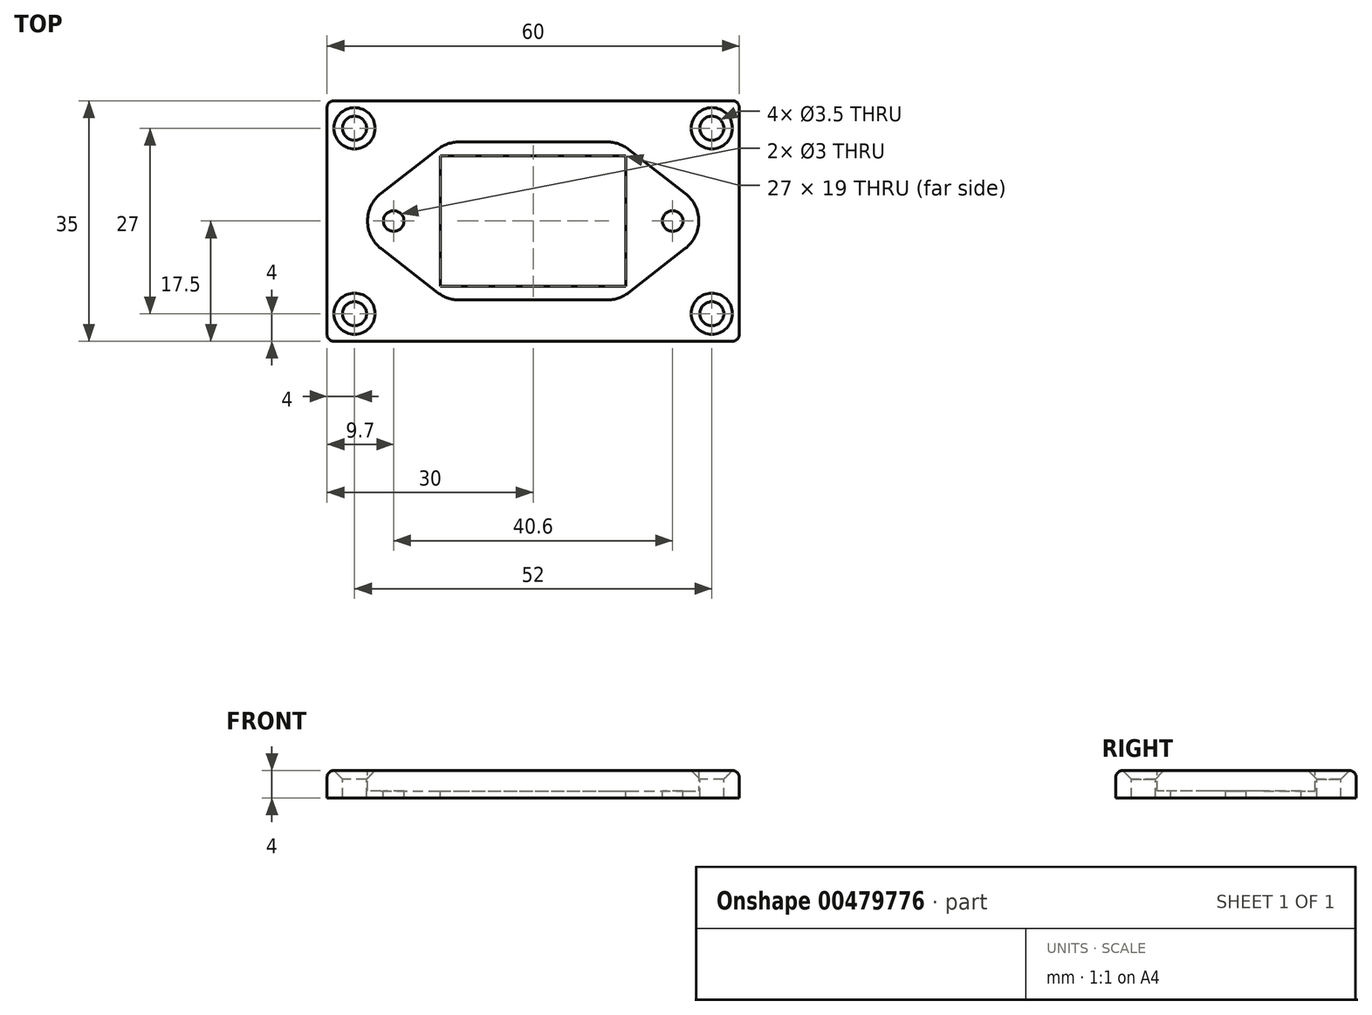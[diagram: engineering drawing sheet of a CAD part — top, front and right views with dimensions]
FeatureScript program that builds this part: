
annotation { "Feature Type Name" : "Feature", "Feature Type Description" : "" }
export const myFeature = defineFeature(function(context is Context, id is Id, definition is map)
    precondition{}
    {
        {
            var Q0;
            Q0=qCreatedBy(makeId("Top.planeOp"),FACE);
            var sketch = newSketch(context, id + "F0", { "sketchPlane" : qUnion([Q0])});
            skLineSegment(sketch, "E0.bottom", {"start": v(-30, 17.5) * mm, "end": v(30, 17.5) * mm});
            skLineSegment(sketch, "E0.top", {"start": v(-30, -17.5) * mm, "end": v(30, -17.5) * mm});
            skLineSegment(sketch, "E0.left", {"start": v(-30, 17.5) * mm, "end": v(-30, -17.5) * mm});
            skLineSegment(sketch, "E0.right", {"start": v(30, 17.5) * mm, "end": v(30, -17.5) * mm});
            skSolve(sketch);
        }
        {
            var Q0;
            Q0 = qSketchRegion(id + "F0", true);
            extrude(context, id + "F1", {"entities" : qUnion([Q0]), "depth" : 4 * mm});
        }
        {
            var Q0;
            Q0=makeQuery(id+"F1.opExtrude","CAP_FACE",FACE,{"disambiguationData":[OSD([sQuery(id+"F0.wireOp",EDGE,"E0.bottom"),sQuery(id+"F0.wireOp",EDGE,"E0.top"),sQuery(id+"F0.wireOp",EDGE,"E0.left"),sQuery(id+"F0.wireOp",EDGE,"E0.right")])],"isStart":false});
            var sketch = newSketch(context, id + "F2", { "sketchPlane" : qUnion([Q0])});
            skLineSegment(sketch, "E1", {"start": v(-12.5, -11.5) * mm, "end": v(12.5, -11.5) * mm});
            skLineSegment(sketch, "E2", {"start": v(-12.5, 11.5) * mm, "end": v(12.5, 11.5) * mm});
            skLineSegment(sketch, "E3", {"start": v(12.5, -11.5) * mm, "end": v(27.3, 0) * mm});
            skLineSegment(sketch, "E4", {"start": v(27.3, 0) * mm, "end": v(12.5, 11.5) * mm});
            skLineSegment(sketch, "E5", {"start": v(-27.3, 0) * mm, "end": v(-12.5, 11.5) * mm});
            skLineSegment(sketch, "E6", {"start": v(-27.3, 0) * mm, "end": v(-12.5, -11.5) * mm});
            skSolve(sketch);
        }
        {
            var Q0;
            Q0 = qSketchRegion(id + "F2", true);
            extrude(context, id + "F3", {"entities" : qUnion([Q0]), "operationType" : NewBodyOperationType.REMOVE, "oppositeDirection" : true, "depth" : 3 * mm});
        }
        {
            var Q0;
            Q0=makeQuery(id+"F3.boolean.opBoolean","COPY",EDGE,{"derivedFrom":makeQuery(id+"F3.opExtrude","SWEPT_EDGE",EDGE,{"disambiguationData":[OSD([sQuery(id+"F2.wireOp",EDGE,"E2"),sQuery(id+"F2.wireOp",EDGE,"E4")])]})});
            var Q1;
            Q1=makeQuery(id+"F3.boolean.opBoolean","COPY",EDGE,{"derivedFrom":makeQuery(id+"F3.opExtrude","SWEPT_EDGE",EDGE,{"disambiguationData":[OSD([sQuery(id+"F2.wireOp",EDGE,"E1"),sQuery(id+"F2.wireOp",EDGE,"E3")])]})});
            var Q2;
            Q2=makeQuery(id+"F3.boolean.opBoolean","COPY",EDGE,{"derivedFrom":makeQuery(id+"F3.opExtrude","SWEPT_EDGE",EDGE,{"disambiguationData":[OSD([sQuery(id+"F2.wireOp",EDGE,"E1"),sQuery(id+"F2.wireOp",EDGE,"E6")])]})});
            var Q3;
            Q3=makeQuery(id+"F3.boolean.opBoolean","COPY",EDGE,{"derivedFrom":makeQuery(id+"F3.opExtrude","SWEPT_EDGE",EDGE,{"disambiguationData":[OSD([sQuery(id+"F2.wireOp",EDGE,"E2"),sQuery(id+"F2.wireOp",EDGE,"E5")])]})});
            var Q4;
            Q4=makeQuery(id+"F3.boolean.opBoolean","COPY",EDGE,{"derivedFrom":makeQuery(id+"F3.opExtrude","SWEPT_EDGE",EDGE,{"disambiguationData":[OSD([sQuery(id+"F2.wireOp",EDGE,"E3"),sQuery(id+"F2.wireOp",EDGE,"E4")])]})});
            var Q5;
            Q5=makeQuery(id+"F3.boolean.opBoolean","COPY",EDGE,{"derivedFrom":makeQuery(id+"F3.opExtrude","SWEPT_EDGE",EDGE,{"disambiguationData":[OSD([sQuery(id+"F2.wireOp",EDGE,"E5"),sQuery(id+"F2.wireOp",EDGE,"E6")])]})});
            fillet(context, id + "F4", {"entities" : qUnion([Q0, Q1, Q2, Q3, Q4, Q5]), "radius" : 5.08 * mm, "tangentPropagation" : true, "allowEdgeOverflow" : false});
        }
        {
            var Q0;
            Q0=makeQuery(id+"F3.boolean.opBoolean","COPY",FACE,{"derivedFrom":makeQuery(id+"F3.opExtrude","CAP_FACE",FACE,{"disambiguationData":[OSD([sQuery(id+"F2.wireOp",EDGE,"E1"),sQuery(id+"F2.wireOp",EDGE,"E2"),sQuery(id+"F2.wireOp",EDGE,"E3"),sQuery(id+"F2.wireOp",EDGE,"E4"),sQuery(id+"F2.wireOp",EDGE,"E5"),sQuery(id+"F2.wireOp",EDGE,"E6")])],"isStart":false})});
            var sketch = newSketch(context, id + "F5", { "sketchPlane" : qUnion([Q0])});
            skLineSegment(sketch, "E7.bottom", {"start": v(-13.5, 9.5) * mm, "end": v(13.5, 9.5) * mm});
            skLineSegment(sketch, "E7.top", {"start": v(-13.5, -9.5) * mm, "end": v(13.5, -9.5) * mm});
            skLineSegment(sketch, "E7.left", {"start": v(-13.5, 9.5) * mm, "end": v(-13.5, -9.5) * mm});
            skLineSegment(sketch, "E7.right", {"start": v(13.5, 9.5) * mm, "end": v(13.5, -9.5) * mm});
            skSolve(sketch);
        }
        {
            var Q0;
            Q0 = qSketchRegion(id + "F5", true);
            extrude(context, id + "F6", {"entities" : qUnion([Q0]), "operationType" : NewBodyOperationType.REMOVE, "oppositeDirection" : true, "depth" : 25.4 * mm});
        }
        {
            var Q0;
            Q0=makeQuery(id+"F1.opExtrude","CAP_FACE",FACE,{"disambiguationData":[OSD([sQuery(id+"F0.wireOp",EDGE,"E0.bottom"),sQuery(id+"F0.wireOp",EDGE,"E0.top"),sQuery(id+"F0.wireOp",EDGE,"E0.left"),sQuery(id+"F0.wireOp",EDGE,"E0.right")])],"isStart":false});
            var sketch = newSketch(context, id + "F7", { "sketchPlane" : qUnion([Q0])});
            skPoint(sketch, "E8", {"position": v(-26, 13.5) * mm});
            skPoint(sketch, "E9", {"position": v(26, 13.5) * mm});
            skPoint(sketch, "E10", {"position": v(26, -13.5) * mm});
            skPoint(sketch, "E11", {"position": v(-26, -13.5) * mm});
            skPoint(sketch, "E12", {"position": v(-20.3, 0) * mm});
            skPoint(sketch, "E13", {"position": v(20.3, 0) * mm});
            skSolve(sketch);
        }
        {
            var Q0;
            Q0=sQuery(id+"F7.wireOp",VERTEX,"E8");
            var Q1;
            Q1=sQuery(id+"F7.wireOp",VERTEX,"E9");
            var Q2;
            Q2=sQuery(id+"F7.wireOp",VERTEX,"E10");
            var Q3;
            Q3=sQuery(id+"F7.wireOp",VERTEX,"E11");
            var Q4;
            Q4=makeQuery(id+"F1.opExtrude","SWEPT_BODY",BODY,{"disambiguationData":[OSD([sQuery(id+"F0.wireOp",EDGE,"E0.bottom"),sQuery(id+"F0.wireOp",EDGE,"E0.top"),sQuery(id+"F0.wireOp",EDGE,"E0.left"),sQuery(id+"F0.wireOp",EDGE,"E0.right")])]});
            hole(context, id + "F8", {"style" : HoleStyle.C_SINK, "endStyle" : HoleEndStyle.THROUGH, "holeDiameter" : 3.5 * mm, "cSinkDiameter" : 6 * mm, "cSinkAngle" : 90 * degree, "isTappedThrough" : true, "tappedDepth" : 12.7 * mm, "tapClearance" : 3, "locations" : qUnion([Q0, Q1, Q2, Q3]), "scope" : qUnion([Q4])});
        }
        {
            var Q0;
            Q0=sQuery(id+"F7.wireOp",VERTEX,"E12");
            var Q1;
            Q1=sQuery(id+"F7.wireOp",VERTEX,"E13");
            var Q2;
            Q2=makeQuery(id+"F1.opExtrude","SWEPT_BODY",BODY,{"disambiguationData":[OSD([sQuery(id+"F0.wireOp",EDGE,"E0.bottom"),sQuery(id+"F0.wireOp",EDGE,"E0.top"),sQuery(id+"F0.wireOp",EDGE,"E0.left"),sQuery(id+"F0.wireOp",EDGE,"E0.right")])]});
            hole(context, id + "F9", {"style" : HoleStyle.SIMPLE, "endStyle" : HoleEndStyle.THROUGH, "holeDiameter" : 3 * mm, "isTappedThrough" : true, "tappedDepth" : 12.7 * mm, "tapClearance" : 3, "locations" : qUnion([Q0, Q1]), "scope" : qUnion([Q2])});
        }
        {
            var Q0;
            Q0=makeQuery(id+"F1.opExtrude","CAP_EDGE",EDGE,{"disambiguationData":[OSD([sQuery(id+"F0.wireOp",EDGE,"E0.bottom")])],"isStart":false});
            var Q1;
            Q1=makeQuery(id+"F1.opExtrude","CAP_EDGE",EDGE,{"disambiguationData":[OSD([sQuery(id+"F0.wireOp",EDGE,"E0.left")])],"isStart":false});
            var Q2;
            Q2=makeQuery(id+"F1.opExtrude","CAP_EDGE",EDGE,{"disambiguationData":[OSD([sQuery(id+"F0.wireOp",EDGE,"E0.top")])],"isStart":false});
            var Q3;
            Q3=makeQuery(id+"F1.opExtrude","CAP_EDGE",EDGE,{"disambiguationData":[OSD([sQuery(id+"F0.wireOp",EDGE,"E0.right")])],"isStart":false});
            var Q4;
            Q4=makeQuery(id+"F1.opExtrude","SWEPT_EDGE",EDGE,{"disambiguationData":[OSD([sQuery(id+"F0.wireOp",EDGE,"E0.top"),sQuery(id+"F0.wireOp",EDGE,"E0.right")])]});
            var Q5;
            Q5=makeQuery(id+"F1.opExtrude","SWEPT_EDGE",EDGE,{"disambiguationData":[OSD([sQuery(id+"F0.wireOp",EDGE,"E0.bottom"),sQuery(id+"F0.wireOp",EDGE,"E0.right")])]});
            var Q6;
            Q6=makeQuery(id+"F1.opExtrude","SWEPT_EDGE",EDGE,{"disambiguationData":[OSD([sQuery(id+"F0.wireOp",EDGE,"E0.top"),sQuery(id+"F0.wireOp",EDGE,"E0.left")])]});
            var Q7;
            Q7=makeQuery(id+"F1.opExtrude","SWEPT_EDGE",EDGE,{"disambiguationData":[OSD([sQuery(id+"F0.wireOp",EDGE,"E0.bottom"),sQuery(id+"F0.wireOp",EDGE,"E0.left")])]});
            fillet(context, id + "F10", {"entities" : qUnion([Q0, Q1, Q2, Q3, Q4, Q5, Q6, Q7]), "radius" : 1 * mm, "tangentPropagation" : true, "allowEdgeOverflow" : false});
        }
    });
